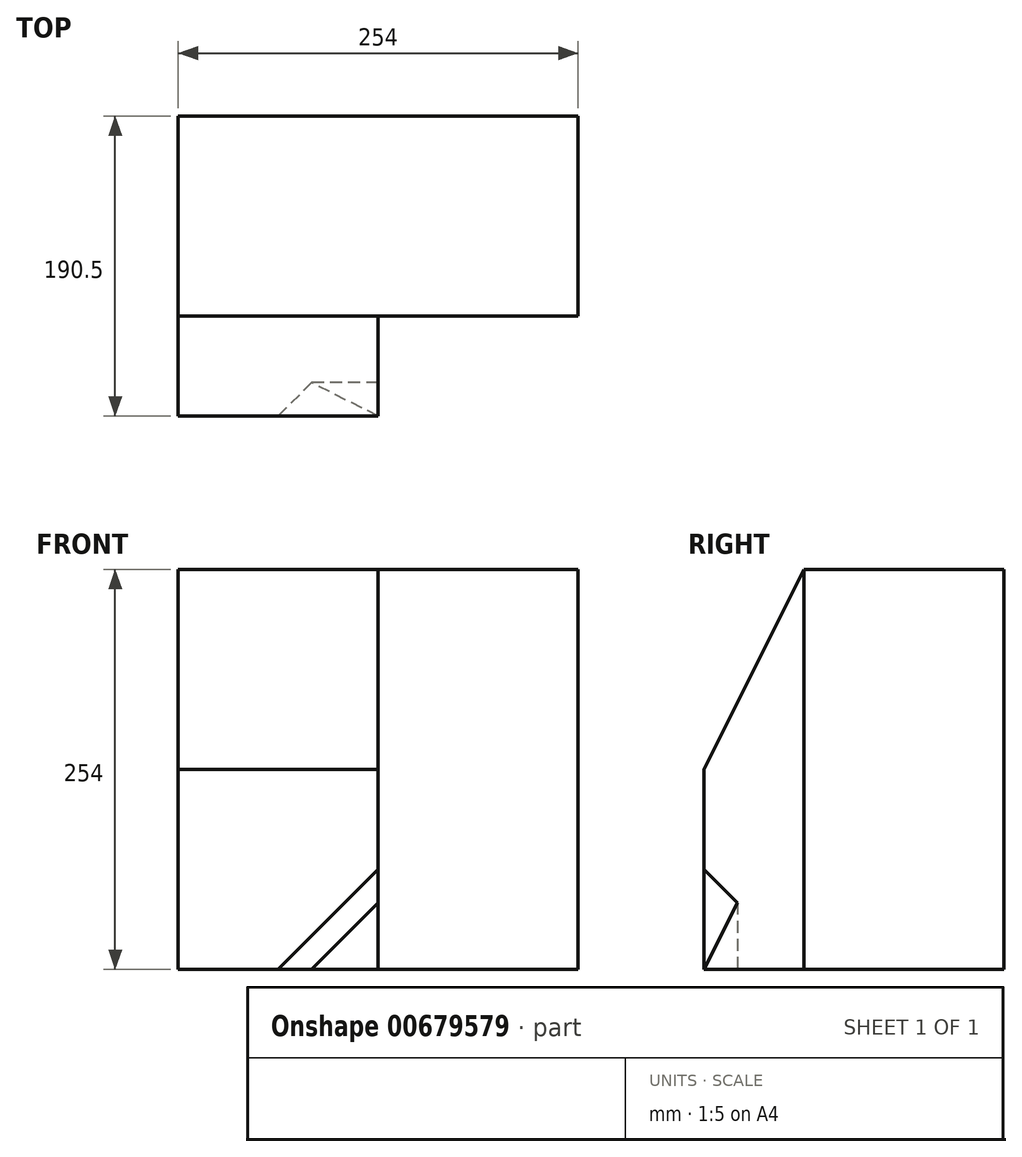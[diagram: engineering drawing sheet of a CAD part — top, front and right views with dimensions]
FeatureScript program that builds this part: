
annotation { "Feature Type Name" : "Feature", "Feature Type Description" : "" }
export const myFeature = defineFeature(function(context is Context, id is Id, definition is map)
    precondition{}
    {
        {
            var Q0;
            Q0=qCreatedBy(makeId("Front.planeOp"),FACE);
            var sketch = newSketch(context, id + "F0", { "sketchPlane" : qUnion([Q0])});
            skLineSegment(sketch, "E0", {"start": v(0, 0) * mm, "end": v(254, 0) * mm});
            skLineSegment(sketch, "E1", {"start": v(254, 0) * mm, "end": v(254, 254) * mm});
            skLineSegment(sketch, "E2", {"start": v(254, 254) * mm, "end": v(0, 254) * mm});
            skLineSegment(sketch, "E3", {"start": v(0, 254) * mm, "end": v(0, 0) * mm});
            skLineSegment(sketch, "E4", {"start": v(127, 254) * mm, "end": v(127, 0) * mm});
            skLineSegment(sketch, "E5", {"start": v(127, 0) * mm, "end": v(254, 127) * mm});
            skSolve(sketch);
        }
        {
            var Q0;
            {var subQ0=sQuery(id+"F0.wireOp",EDGE,"E3");Q0=makeQuery(id+"F0.imprint","IMPRINT",FACE,{"disambiguationData":[TD([[makeQuery(id+"F0.imprint","IMPRINT",EDGE,{"derivedFrom":subQ0}),1.0]])]});}
            extrude(context, id + "F1", {"entities" : qUnion([Q0]), "depth" : 127 * mm, "offsetDistance" : 25.4 * mm});
        }
        {
            var Q0;
            {var subQ4=sQuery(id+"F0.wireOp",EDGE,"E4");Q0=makeQuery(id+"F0.imprint","IMPRINT",FACE,{"disambiguationData":[TD([[makeQuery(id+"F0.imprint","IMPRINT",EDGE,{"derivedFrom":subQ4}),1.0]])]});}
            extrude(context, id + "F2", {"entities" : qUnion([Q0]), "operationType" : NewBodyOperationType.ADD, "depth" : 127 * mm, "offsetDistance" : 25.4 * mm});
        }
        {
            var Q0;
            {var subQ0=sQuery(id+"F0.wireOp",EDGE,"E4");var subQ1=sQuery(id+"F0.wireOp",EDGE,"E2");Q0=makeQuery(id+"F2.boolean.opBoolean","MERGE",FACE,{"derivedFrom":[makeQuery(id+"F1.opExtrude","CAP_FACE",FACE,{"disambiguationData":[OSD([sQuery(id+"F0.wireOp",EDGE,"E0"),subQ1,sQuery(id+"F0.wireOp",EDGE,"E3"),subQ0])],"isStart":false}),makeQuery(id+"F2.opExtrude","CAP_FACE",FACE,{"disambiguationData":[OSD([sQuery(id+"F0.wireOp",EDGE,"E1"),subQ1,subQ0,sQuery(id+"F0.wireOp",EDGE,"E5")])],"isStart":false})]});}
            var sketch = newSketch(context, id + "F3", { "sketchPlane" : qUnion([Q0])});
            skLineSegment(sketch, "E6", {"start": v(127, 0) * mm, "end": v(127, 254) * mm});
            skLineSegment(sketch, "E7", {"start": v(0, 127) * mm, "end": v(127, 127) * mm});
            skSolve(sketch);
        }
        {
            var Q0;
            {var subQ2=sQuery(id+"F3.wireOp",EDGE,"E7");Q0=makeQuery(id+"F3.imprint","IMPRINT",FACE,{"disambiguationData":[TD([[makeQuery(id+"F3.imprint","IMPRINT",EDGE,{"derivedFrom":subQ2}),-1.0]])]});}
            extrude(context, id + "F4", {"entities" : qUnion([Q0]), "operationType" : NewBodyOperationType.ADD, "depth" : 63.5 * mm, "offsetDistance" : 25.4 * mm});
        }
        {
            var Q0;
            {var subQ0=sQuery(id+"F0.wireOp",EDGE,"E3");Q0=makeQuery(id+"F4.boolean.opBoolean","MERGE",FACE,{"derivedFrom":[makeQuery(id+"F1.opExtrude","SWEPT_FACE",FACE,{"disambiguationData":[OSD([subQ0])]}),makeQuery(id+"F4.opExtrude","SWEPT_FACE",FACE,{"disambiguationData":[OSD([subQ0])]})]});}
            var sketch = newSketch(context, id + "F5", { "sketchPlane" : qUnion([Q0])});
            skLineSegment(sketch, "E8", {"start": v(190.5, 127) * mm, "end": v(127, 254) * mm});
            skSolve(sketch);
        }
        {
            var Q0;
            Q0=makeQuery(id+"F5.imprint","IMPRINT",FACE,{"disambiguationData":[TD([[makeQuery(id+"F5.imprint","IMPRINT",EDGE,{"derivedFrom":sQuery(id+"F5.wireOp",EDGE,"E8")}),1.0]])]});
            extrude(context, id + "F6", {"entities" : qUnion([Q0]), "operationType" : NewBodyOperationType.ADD, "oppositeDirection" : true, "depth" : 127 * mm, "offsetDistance" : 25.4 * mm});
        }
        {
            var Q0;
            {var subQ3=sQuery(id+"F0.wireOp",EDGE,"E5");Q0=makeQuery(id+"F0.imprint","IMPRINT",FACE,{"disambiguationData":[TD([[makeQuery(id+"F0.imprint","IMPRINT",EDGE,{"derivedFrom":subQ3}),-1.0]])]});}
            extrude(context, id + "F7", {"entities" : qUnion([Q0]), "operationType" : NewBodyOperationType.ADD, "depth" : 127 * mm, "offsetDistance" : 25.4 * mm});
        }
        {
            var Q0;
            {var subQ0=sQuery(id+"F0.wireOp",EDGE,"E5");var subQ1=sQuery(id+"F0.wireOp",EDGE,"E1");var subQ2=sQuery(id+"F0.wireOp",EDGE,"E0");var subQ3=sQuery(id+"F0.wireOp",EDGE,"E4");var subQ4=sQuery(id+"F0.wireOp",EDGE,"E2");Q0=makeQuery(id+"F7.boolean.opBoolean","MERGE",FACE,{"derivedFrom":[makeQuery(id+"F2.boolean.opBoolean","MERGE",FACE,{"derivedFrom":[makeQuery(id+"F1.opExtrude","CAP_FACE",FACE,{"disambiguationData":[OSD([subQ2,subQ4,sQuery(id+"F0.wireOp",EDGE,"E3"),subQ3])],"isStart":false}),makeQuery(id+"F2.opExtrude","CAP_FACE",FACE,{"disambiguationData":[OSD([subQ1,subQ4,subQ3,subQ0])],"isStart":false})]}),makeQuery(id+"F7.opExtrude","CAP_FACE",FACE,{"disambiguationData":[OSD([subQ2,subQ1,subQ0])],"isStart":false})]});}
            var sketch = newSketch(context, id + "F8", { "sketchPlane" : qUnion([Q0])});
            skLineSegment(sketch, "E9", {"start": v(254, 127) * mm, "end": v(127, 127) * mm});
            skLineSegment(sketch, "E10", {"start": v(254, 127) * mm, "end": v(127, 0) * mm});
            skSolve(sketch);
        }
        {
            var Q0;
            Q0=sQuery(id+"F8.wireOp",VERTEX,"E10.end");
            var Q1;
            Q1=sQuery(id+"F8.wireOp",VERTEX,"E9.start");
            var Q2;
            Q2=makeQuery(id+"F7.opExtrude","CAP_VERTEX",VERTEX,{"disambiguationData":[OSD([sQuery(id+"F0.wireOp",EDGE,"E0"),sQuery(id+"F0.wireOp",EDGE,"E1")])],"isStart":true});
            cPlane(context, id + "F9", {"entities" : qUnion([Q0, Q1, Q2]), "cplaneType" : CPlaneType.THREE_POINT, "offset" : 25.4 * mm, "width" : 152.4 * mm, "height" : 152.4 * mm});
        }
        {
            var Q0;
            Q0=qCreatedBy(id+"F9.planeOp",FACE);
            var sketch = newSketch(context, id + "F10", { "sketchPlane" : qUnion([Q0])});
            skLineSegment(sketch, "E11", {"start": v(-51.85, 269.4) * mm, "end": v(-51.85, 89.8) * mm});
            skLineSegment(sketch, "E12", {"start": v(103.7, 179.6) * mm, "end": v(-51.85, 89.8) * mm});
            skLineSegment(sketch, "E13", {"start": v(-51.85, 269.4) * mm, "end": v(103.7, 179.6) * mm});
            skSolve(sketch);
        }
        {
            var Q0;
            Q0 = qSketchRegion(id + "F10", true);
            extrude(context, id + "F11", {"entities" : qUnion([Q0]), "operationType" : NewBodyOperationType.REMOVE, "depth" : 172.21 * mm, "offsetDistance" : 25.4 * mm});
        }
    });
